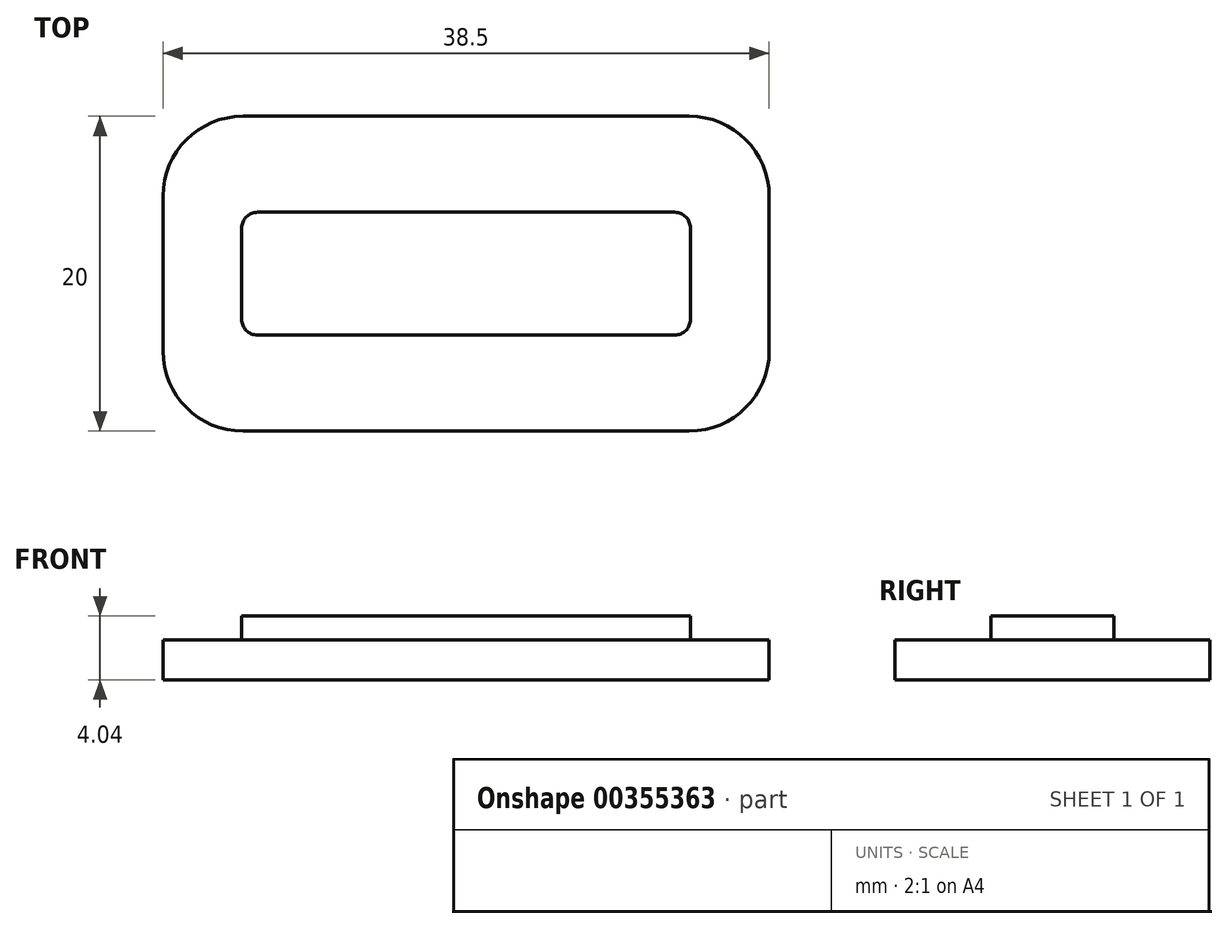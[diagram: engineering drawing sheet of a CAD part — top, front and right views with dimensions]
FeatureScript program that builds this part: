
annotation { "Feature Type Name" : "Feature", "Feature Type Description" : "" }
export const myFeature = defineFeature(function(context is Context, id is Id, definition is map)
    precondition{}
    {
        {
            var Q0;
            Q0=qCreatedBy(makeId("Front.planeOp"),FACE);
            var sketch = newSketch(context, id + "F0", { "sketchPlane" : qUnion([Q0])});
            skLineSegment(sketch, "E0.bottom", {"start": v(14.25, -0.75) * mm, "end": v(-14.25, -0.75) * mm});
            skLineSegment(sketch, "E0.top", {"start": v(14.25, 0.75) * mm, "end": v(-14.25, 0.75) * mm});
            skLineSegment(sketch, "E0.left", {"start": v(14.25, -0.75) * mm, "end": v(14.25, 0.75) * mm});
            skLineSegment(sketch, "E0.right", {"start": v(-14.25, -0.75) * mm, "end": v(-14.25, 0.75) * mm});
            skPoint(sketch, "E0.middle", {"position": v(0, 0) * mm});
            skLineSegment(sketch, "E1.bottom", {"start": v(19.25, -3.29) * mm, "end": v(-19.25, -3.29) * mm});
            skLineSegment(sketch, "E1.top", {"start": v(19.25, -0.75) * mm, "end": v(-19.25, -0.75) * mm});
            skLineSegment(sketch, "E1.left", {"start": v(19.25, -3.29) * mm, "end": v(19.25, -0.75) * mm});
            skLineSegment(sketch, "E1.right", {"start": v(-19.25, -3.29) * mm, "end": v(-19.25, -0.75) * mm});
            skPoint(sketch, "E1.middle", {"position": v(0, -2.02) * mm});
            skSolve(sketch);
        }
        {
            var Q0;
            Q0=makeQuery(id+"F0.imprint","IMPRINT",FACE,{"disambiguationData":[TD([[makeQuery(id+"F0.imprint","IMPRINT",EDGE,{"derivedFrom":sQuery(id+"F0.wireOp",EDGE,"E0.top")}),1.0]])]});
            extrude(context, id + "F1", {"entities" : qUnion([Q0]), "endBound" : BoundingType.SYMMETRIC, "depth" : 7.8 * mm});
        }
        {
            var Q0;
            Q0=makeQuery(id+"F1.opExtrude","CAP_EDGE",EDGE,{"disambiguationData":[OSD([sQuery(id+"F0.wireOp",EDGE,"E0.right")])],"isStart":false});
            var Q1;
            Q1=makeQuery(id+"F1.opExtrude","CAP_EDGE",EDGE,{"disambiguationData":[OSD([sQuery(id+"F0.wireOp",EDGE,"E0.right")])],"isStart":true});
            var Q2;
            Q2=makeQuery(id+"F1.opExtrude","CAP_EDGE",EDGE,{"disambiguationData":[OSD([sQuery(id+"F0.wireOp",EDGE,"E0.left")])],"isStart":true});
            var Q3;
            Q3=makeQuery(id+"F1.opExtrude","CAP_EDGE",EDGE,{"disambiguationData":[OSD([sQuery(id+"F0.wireOp",EDGE,"E0.left")])],"isStart":false});
            fillet(context, id + "F2", {"entities" : qUnion([Q0, Q1, Q2, Q3]), "radius" : 1 * mm, "tangentPropagation" : true, "allowEdgeOverflow" : false});
        }
        {
            var Q0;
            Q0=makeQuery(id+"F0.imprint","IMPRINT",FACE,{"disambiguationData":[TD([[makeQuery(id+"F0.imprint","IMPRINT",EDGE,{"derivedFrom":sQuery(id+"F0.wireOp",EDGE,"E1.bottom")}),-1.0]])]});
            extrude(context, id + "F3", {"entities" : qUnion([Q0]), "endBound" : BoundingType.SYMMETRIC, "depth" : 20 * mm});
        }
        {
            var Q0;
            Q0=makeQuery(id+"F3.opExtrude","CAP_EDGE",EDGE,{"disambiguationData":[OSD([sQuery(id+"F0.wireOp",EDGE,"E1.right")])],"isStart":false});
            var Q1;
            Q1=makeQuery(id+"F3.opExtrude","CAP_EDGE",EDGE,{"disambiguationData":[OSD([sQuery(id+"F0.wireOp",EDGE,"E1.left")])],"isStart":false});
            var Q2;
            Q2=makeQuery(id+"F3.opExtrude","CAP_EDGE",EDGE,{"disambiguationData":[OSD([sQuery(id+"F0.wireOp",EDGE,"E1.left")])],"isStart":true});
            var Q3;
            Q3=makeQuery(id+"F3.opExtrude","CAP_EDGE",EDGE,{"disambiguationData":[OSD([sQuery(id+"F0.wireOp",EDGE,"E1.right")])],"isStart":true});
            fillet(context, id + "F4", {"entities" : qUnion([Q0, Q1, Q2, Q3]), "radius" : 5.08 * mm, "tangentPropagation" : true, "allowEdgeOverflow" : false});
        }
    });
